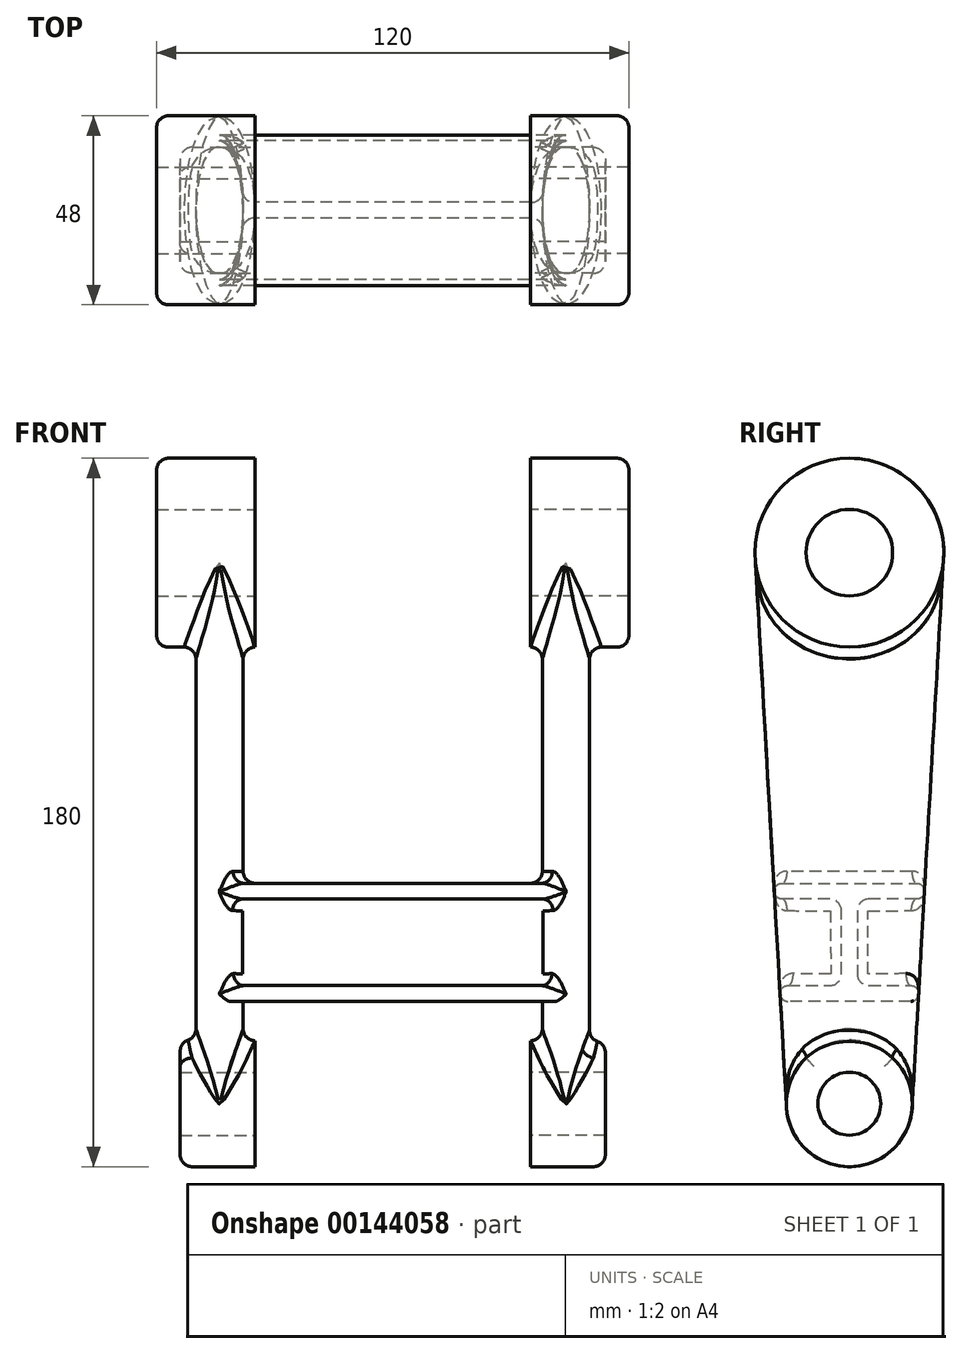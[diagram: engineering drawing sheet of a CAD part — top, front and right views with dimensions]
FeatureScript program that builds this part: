
annotation { "Feature Type Name" : "Feature", "Feature Type Description" : "" }
export const myFeature = defineFeature(function(context is Context, id is Id, definition is map)
    precondition{}
    {
        {
            assignVariable(context, id + "F0", {"name" : "gap", "anyValue" : 70 * mm});
        }
        {
            var Q0;
            Q0=qCreatedBy(makeId("Right.planeOp"),FACE);
            var sketch = newSketch(context, id + "F1", { "sketchPlane" : qUnion([Q0])});
            skCircle(sketch, "E0", {"center": v(0, 0) * mm, "radius": 8 * mm});
            skCircle(sketch, "E1", {"center": v(0, 0) * mm, "radius": 16 * mm});
            skCircle(sketch, "E2", {"center": v(0, 140) * mm, "radius": 11 * mm});
            skCircle(sketch, "E3", {"center": v(0, 140) * mm, "radius": 24 * mm});
            skSolve(sketch);
        }
        {
            var Q0;
            Q0=makeQuery(id+"F1.imprint","IMPRINT",FACE,{"disambiguationData":[TD([[makeQuery(id+"F1.imprint","IMPRINT",EDGE,{"derivedFrom":sQuery(id+"F1.wireOp",EDGE,"E0")}),1.0]])]});
            var Q1;
            Q1=makeQuery(id+"F1.imprint","IMPRINT",FACE,{"disambiguationData":[TD([[makeQuery(id+"F1.imprint","IMPRINT",EDGE,{"derivedFrom":sQuery(id+"F1.wireOp",EDGE,"E0")}),-1.0]])]});
            extrude(context, id + "F2", {"entities" : qUnion([Q0, Q1]), "depth" : 19 * mm});
        }
        {
            var Q0;
            Q0=makeQuery(id+"F1.imprint","IMPRINT",FACE,{"disambiguationData":[TD([[makeQuery(id+"F1.imprint","IMPRINT",EDGE,{"derivedFrom":sQuery(id+"F1.wireOp",EDGE,"E2")}),1.0]])]});
            var Q1;
            Q1=makeQuery(id+"F1.imprint","IMPRINT",FACE,{"disambiguationData":[TD([[makeQuery(id+"F1.imprint","IMPRINT",EDGE,{"derivedFrom":sQuery(id+"F1.wireOp",EDGE,"E2")}),-1.0]])]});
            extrude(context, id + "F3", {"entities" : qUnion([Q0, Q1]), "depth" : 25 * mm});
        }
        {
            var Q0;
            Q0=qCreatedBy(makeId("Top.planeOp"),FACE);
            var sketch = newSketch(context, id + "F4", { "sketchPlane" : qUnion([Q0])});
            skEllipse(sketch, "E4", {"center": v(9, 0) * mm, "majorRadius": 16 * mm, "minorRadius": 6 * mm, "majorAxis": v(0, -1)});
            skPoint(sketch, "E5", {"position": v(3, 0) * mm});
            skLineSegment(sketch, "E6", {"start": v(0, 16) * mm, "end": v(19, 16) * mm, "construction": true});
            skSolve(sketch);
        }
        {
            var Q0;
            Q0=sQuery(id+"F1.wireOp",VERTEX,"E3.center");
            var Q1;
            Q1=qCreatedBy(makeId("Top.planeOp"),FACE);
            cPlane(context, id + "F5", {"entities" : qUnion([Q0, Q1]), "cplaneType" : CPlaneType.PLANE_POINT, "offset" : 25 * mm, "width" : 150 * mm, "height" : 150 * mm});
        }
        {
            var Q0;
            Q0=qCreatedBy(id+"F5.planeOp",FACE);
            var sketch = newSketch(context, id + "F6", { "sketchPlane" : qUnion([Q0])});
            skEllipse(sketch, "E7", {"center": v(9, 0) * mm, "majorRadius": 24 * mm, "minorRadius": 6 * mm, "majorAxis": v(0, 1)});
            skPoint(sketch, "E8", {"position": v(3, 0) * mm});
            skLineSegment(sketch, "E9", {"start": v(0, 24) * mm, "end": v(25, 24) * mm, "construction": true});
            skSolve(sketch);
        }
        {
            var Q0;
            Q0=makeQuery(id+"F6.imprint","IMPRINT",FACE,{"disambiguationData":[TD([[makeQuery(id+"F6.imprint","IMPRINT",EDGE,{"derivedFrom":sQuery(id+"F6.wireOp",EDGE,"E7")}),1.0]])]});
            var Q1;
            Q1=makeQuery(id+"F4.imprint","IMPRINT",FACE,{"disambiguationData":[TD([[makeQuery(id+"F4.imprint","IMPRINT",EDGE,{"derivedFrom":sQuery(id+"F4.wireOp",EDGE,"E4")}),1.0]])]});
            loft(context, id + "F7", {"operationType" : NewBodyOperationType.ADD, "sheetProfilesArray" : [{ "sheetProfileEntities" : qUnion([Q0]) }, { "sheetProfileEntities" : qUnion([Q1]) }]});
        }
        {
            var Q0;
            Q0=makeQuery(id+"F1.imprint","IMPRINT",FACE,{"disambiguationData":[TD([[makeQuery(id+"F1.imprint","IMPRINT",EDGE,{"derivedFrom":sQuery(id+"F1.wireOp",EDGE,"E2")}),1.0]])]});
            var Q1;
            Q1=makeQuery(id+"F1.imprint","IMPRINT",FACE,{"disambiguationData":[TD([[makeQuery(id+"F1.imprint","IMPRINT",EDGE,{"derivedFrom":sQuery(id+"F1.wireOp",EDGE,"E0")}),1.0]])]});
            extrude(context, id + "F8", {"entities" : qUnion([Q0, Q1]), "operationType" : NewBodyOperationType.REMOVE, "depth" : 25 * mm});
        }
        {
            var Q0;
            Q0=sQuery(id+"F4.wireOp",VERTEX,"E4.center");
            var Q1;
            Q1=qCreatedBy(makeId("Right.planeOp"),FACE);
            cPlane(context, id + "F9", {"entities" : qUnion([Q0, Q1]), "cplaneType" : CPlaneType.PLANE_POINT, "offset" : 25 * mm, "width" : 150 * mm, "height" : 150 * mm});
        }
        {
            var Q0;
            Q0=qCreatedBy(makeId("Right.planeOp"),FACE);
            cPlane(context, id + "F10", {"entities" : qUnion([Q0]), "cplaneType" : CPlaneType.OFFSET, "offset" : getVariable(context, 'gap') / 2, "oppositeDirection" : true, "width" : 150 * mm, "height" : 150 * mm});
        }
        {
            var Q0;
            Q0=makeQuery(id+"F2.opExtrude","SWEPT_BODY",BODY,{"disambiguationData":[OSD([sQuery(id+"F1.wireOp",EDGE,"E1")])]});
            var Q1;
            Q1=qCreatedBy(id+"F10.planeOp",FACE);
            mirror(context, id + "F11", {"entities" : qUnion([Q0]), "mirrorPlane" : qUnion([Q1])});
        }
        {
            var Q0;
            Q0=qCreatedBy(makeId("Right.planeOp"),FACE);
            var sketch = newSketch(context, id + "F12", { "sketchPlane" : qUnion([Q0])});
            skLineSegment(sketch, "E10", {"start": v(23.96, 138.63) * mm, "end": v(15.97, -0.91) * mm, "construction": true});
            skLineSegment(sketch, "E11", {"start": v(17.51, 26) * mm, "end": v(-15.6, 26) * mm});
            skLineSegment(sketch, "E12", {"start": v(-15.6, 26) * mm, "end": v(-15.6, 30) * mm, "construction": true});
            skLineSegment(sketch, "E13", {"start": v(-15.6, 30) * mm, "end": v(-5, 30) * mm});
            skLineSegment(sketch, "E14", {"start": v(-2, 33) * mm, "end": v(-2, 49) * mm});
            skLineSegment(sketch, "E15", {"start": v(-5, 52) * mm, "end": v(-17.1, 52) * mm});
            skLineSegment(sketch, "E16", {"start": v(-17.1, 52) * mm, "end": v(-17.1, 56) * mm, "construction": true});
            skLineSegment(sketch, "E17", {"start": v(-17.1, 56) * mm, "end": v(17.11, 56) * mm});
            skLineSegment(sketch, "E18", {"start": v(17.11, 52) * mm, "end": v(5, 52) * mm});
            skLineSegment(sketch, "E19", {"start": v(2, 49) * mm, "end": v(2, 33) * mm});
            skLineSegment(sketch, "E20", {"start": v(5, 30) * mm, "end": v(17.74, 30) * mm});
            skLineSegment(sketch, "E21", {"start": v(15.63, 30) * mm, "end": v(15.63, 26) * mm, "construction": true});
            skLineSegment(sketch, "E22", {"start": v(-23.96, 138.62) * mm, "end": v(-16, 0) * mm, "construction": true});
            skPoint(sketch, "E23.visualSharp", {"position": v(0, 52) * mm});
            skArc(sketch, "E23.filletArc", {"start": v(5, 52) * mm, "mid": v(2.88, 51.12) * mm, "end": v(2, 49) * mm});
            skPoint(sketch, "E24.visualSharp", {"position": v(-2, 52) * mm});
            skArc(sketch, "E24.filletArc", {"start": v(-2, 49) * mm, "mid": v(-2.88, 51.12) * mm, "end": v(-5, 52) * mm});
            skPoint(sketch, "E25.visualSharp", {"position": v(-2, 30) * mm});
            skArc(sketch, "E25.filletArc", {"start": v(-5, 30) * mm, "mid": v(-2.88, 30.88) * mm, "end": v(-2, 33) * mm});
            skPoint(sketch, "E26.visualSharp", {"position": v(2, 30) * mm});
            skArc(sketch, "E26.filletArc", {"start": v(2, 33) * mm, "mid": v(2.88, 30.88) * mm, "end": v(5, 30) * mm});
            skPoint(sketch, "E27.endSnap0", {"position": v(0, 56) * mm});
            skLineSegment(sketch, "E28", {"start": v(0, 0) * mm, "end": v(0, 93.69) * mm, "construction": true});
            skArc(sketch, "E29", {"start": v(-15.6, 30) * mm, "mid": v(-17.6, 28) * mm, "end": v(-15.6, 26) * mm});
            skArc(sketch, "E30", {"start": v(-17.1, 56) * mm, "mid": v(-19.1, 54) * mm, "end": v(-17.1, 52) * mm});
            skArc(sketch, "E31", {"start": v(17.11, 52) * mm, "mid": v(19.11, 54) * mm, "end": v(17.11, 56) * mm});
            skLineSegment(sketch, "E32", {"start": v(17.11, 52) * mm, "end": v(17.11, 56) * mm, "construction": true});
            skArc(sketch, "E33", {"start": v(15.63, 26) * mm, "mid": v(17.63, 28) * mm, "end": v(15.63, 30) * mm});
            skSolve(sketch);
        }
        {
            var Q0;
            Q0 = qSketchRegion(id + "F12", true);
            var Q1;
            Q1=qCreatedBy(id+"F9.planeOp",FACE);
            var Q2;
            Q2=qCreatedBy(id+"F10.planeOp",FACE);
            var Q3;
            Q3=makeQuery(id+"F11.opPattern","COPY",BODY,{"derivedFrom":makeQuery(id+"F2.opExtrude","SWEPT_BODY",BODY,{"disambiguationData":[OSD([sQuery(id+"F1.wireOp",EDGE,"E1")])]}),"instanceName":"1"});
            extrude(context, id + "F13", {"entities" : qUnion([Q0]), "operationType" : NewBodyOperationType.ADD, "endBound" : BoundingType.UP_TO_SURFACE, "endBoundEntityFace" : qUnion([Q1]), "depth" : 30 * mm, "hasSecondDirection" : true, "secondDirectionBound" : SecondDirectionBoundingType.UP_TO_SURFACE, "secondDirectionOppositeDirection" : true, "secondDirectionBoundEntityFace" : qUnion([Q2]), "secondDirectionBoundEntityBody" : qUnion([Q3]), "secondDirectionDepth" : 25 * mm});
        }
        {
            var Q0;
            Q0=makeQuery(id+"F13.boolean.opBoolean","INTERSECT",EDGE,{"derivedFrom":[makeQuery(id+"F7.opLoft","SWEPT_FACE",FACE,{"disambiguationData":[OSD([sQuery(id+"F4.wireOp",EDGE,"E4"),sQuery(id+"F6.wireOp",EDGE,"E7")])]}),makeQuery(id+"F13.opExtrude","SWEPT_FACE",FACE,{"disambiguationData":[OSD([sQuery(id+"F12.wireOp",EDGE,"E17")])]})]});
            fillet(context, id + "F14", {"entities" : qUnion([Q0]), "radius" : 3 * mm, "tangentPropagation" : true, "allowEdgeOverflow" : false});
        }
        {
            var Q0;
            Q0=makeQuery(id+"F13.boolean.opBoolean","INTERSECT",EDGE,{"derivedFrom":[makeQuery(id+"F7.opLoft","SWEPT_FACE",FACE,{"disambiguationData":[OSD([sQuery(id+"F4.wireOp",EDGE,"E4"),sQuery(id+"F6.wireOp",EDGE,"E7")])]}),makeQuery(id+"F13.opExtrude","SWEPT_FACE",FACE,{"disambiguationData":[OSD([sQuery(id+"F12.wireOp",EDGE,"E13")])]})]});
            var Q1;
            Q1=makeQuery(id+"F13.boolean.opBoolean","INTERSECT",EDGE,{"derivedFrom":[makeQuery(id+"F7.opLoft","SWEPT_FACE",FACE,{"disambiguationData":[OSD([sQuery(id+"F4.wireOp",EDGE,"E4"),sQuery(id+"F6.wireOp",EDGE,"E7")])]}),makeQuery(id+"F13.opExtrude","SWEPT_FACE",FACE,{"disambiguationData":[OSD([sQuery(id+"F12.wireOp",EDGE,"E14")])]})]});
            var Q2;
            Q2=makeQuery(id+"F13.boolean.opBoolean","INTERSECT",EDGE,{"derivedFrom":[makeQuery(id+"F7.opLoft","SWEPT_FACE",FACE,{"disambiguationData":[OSD([sQuery(id+"F4.wireOp",EDGE,"E4"),sQuery(id+"F6.wireOp",EDGE,"E7")])]}),makeQuery(id+"F13.opExtrude","SWEPT_FACE",FACE,{"disambiguationData":[OSD([sQuery(id+"F12.wireOp",EDGE,"E20")])]})]});
            var Q3;
            Q3=makeQuery(id+"F13.boolean.opBoolean","INTERSECT",EDGE,{"derivedFrom":[makeQuery(id+"F7.opLoft","SWEPT_FACE",FACE,{"disambiguationData":[OSD([sQuery(id+"F4.wireOp",EDGE,"E4"),sQuery(id+"F6.wireOp",EDGE,"E7")])]}),makeQuery(id+"F13.opExtrude","SWEPT_FACE",FACE,{"disambiguationData":[OSD([sQuery(id+"F12.wireOp",EDGE,"E19")])]})]});
            fillet(context, id + "F15", {"entities" : qUnion([Q0, Q1, Q2, Q3]), "radius" : 3 * mm, "tangentPropagation" : true, "allowEdgeOverflow" : false});
        }
        {
            var Q0;
            Q0=makeQuery(id+"F2.opExtrude","SWEPT_BODY",BODY,{"disambiguationData":[OSD([sQuery(id+"F1.wireOp",EDGE,"E1")])]});
            var Q1;
            Q1=qCreatedBy(id+"F10.planeOp",FACE);
            mirror(context, id + "F16", {"operationType" : NewBodyOperationType.ADD, "entities" : qUnion([Q0]), "mirrorPlane" : qUnion([Q1])});
        }
        {
            var Q0;
            Q0=makeQuery(id+"F3.opExtrude","CAP_EDGE",EDGE,{"disambiguationData":[OSD([sQuery(id+"F1.wireOp",EDGE,"E3")])],"isStart":false});
            var Q1;
            Q1=makeQuery(id+"F16.opPattern","COPY",EDGE,{"derivedFrom":makeQuery(id+"F3.opExtrude","CAP_EDGE",EDGE,{"disambiguationData":[OSD([sQuery(id+"F1.wireOp",EDGE,"E3")])],"isStart":false}),"instanceName":"1"});
            var Q2;
            Q2=makeQuery(id+"F2.opExtrude","CAP_EDGE",EDGE,{"disambiguationData":[OSD([sQuery(id+"F1.wireOp",EDGE,"E1")])],"isStart":false});
            var Q3;
            Q3=makeQuery(id+"F16.opPattern","COPY",EDGE,{"derivedFrom":makeQuery(id+"F2.opExtrude","CAP_EDGE",EDGE,{"disambiguationData":[OSD([sQuery(id+"F1.wireOp",EDGE,"E1")])],"isStart":false}),"instanceName":"1"});
            fillet(context, id + "F17", {"entities" : qUnion([Q0, Q1, Q2, Q3]), "radius" : 3 * mm, "tangentPropagation" : true, "allowEdgeOverflow" : false});
        }
        {
            var Q0;
            Q0=makeQuery(id+"F7.boolean.opBoolean","INTERSECT",EDGE,{"derivedFrom":[makeQuery(id+"F3.opExtrude","SWEPT_FACE",FACE,{"disambiguationData":[OSD([sQuery(id+"F1.wireOp",EDGE,"E3")])]}),makeQuery(id+"F7.opLoft","SWEPT_FACE",FACE,{"disambiguationData":[OSD([sQuery(id+"F4.wireOp",EDGE,"E4"),sQuery(id+"F6.wireOp",EDGE,"E7")])]})]});
            var Q1;
            Q1=makeQuery(id+"F11.opPattern","COPY",EDGE,{"derivedFrom":makeQuery(id+"F7.boolean.opBoolean","INTERSECT",EDGE,{"derivedFrom":[makeQuery(id+"F3.opExtrude","SWEPT_FACE",FACE,{"disambiguationData":[OSD([sQuery(id+"F1.wireOp",EDGE,"E3")])]}),makeQuery(id+"F7.opLoft","SWEPT_FACE",FACE,{"disambiguationData":[OSD([sQuery(id+"F4.wireOp",EDGE,"E4"),sQuery(id+"F6.wireOp",EDGE,"E7")])]})]}),"instanceName":"1"});
            var Q2;
            Q2=makeQuery(id+"F11.opPattern","COPY",EDGE,{"derivedFrom":makeQuery(id+"F7.boolean.opBoolean","INTERSECT",EDGE,{"derivedFrom":[makeQuery(id+"F2.opExtrude","SWEPT_FACE",FACE,{"disambiguationData":[OSD([sQuery(id+"F1.wireOp",EDGE,"E1")])]}),makeQuery(id+"F7.opLoft","SWEPT_FACE",FACE,{"disambiguationData":[OSD([sQuery(id+"F4.wireOp",EDGE,"E4"),sQuery(id+"F6.wireOp",EDGE,"E7")])]})]}),"instanceName":"1"});
            var Q3;
            Q3=makeQuery(id+"F7.boolean.opBoolean","INTERSECT",EDGE,{"derivedFrom":[makeQuery(id+"F2.opExtrude","SWEPT_FACE",FACE,{"disambiguationData":[OSD([sQuery(id+"F1.wireOp",EDGE,"E1")])]}),makeQuery(id+"F7.opLoft","SWEPT_FACE",FACE,{"disambiguationData":[OSD([sQuery(id+"F4.wireOp",EDGE,"E4"),sQuery(id+"F6.wireOp",EDGE,"E7")])]})]});
            fillet(context, id + "F18", {"entities" : qUnion([Q0, Q1, Q2, Q3]), "radius" : 3 * mm, "tangentPropagation" : true, "allowEdgeOverflow" : false});
        }
        {
            var Q0;
            Q0=makeQuery(id+"F11.opPattern","COPY",EDGE,{"derivedFrom":makeQuery(id+"F2.opExtrude","CAP_EDGE",EDGE,{"disambiguationData":[OSD([sQuery(id+"F1.wireOp",EDGE,"E1")])],"isStart":false}),"instanceName":"1"});
            var Q1;
            Q1=makeQuery(id+"F11.opPattern","COPY",EDGE,{"derivedFrom":makeQuery(id+"F3.opExtrude","CAP_EDGE",EDGE,{"disambiguationData":[OSD([sQuery(id+"F1.wireOp",EDGE,"E3")])],"isStart":false}),"instanceName":"1"});
            fillet(context, id + "F19", {"entities" : qUnion([Q0, Q1]), "radius" : 3 * mm, "tangentPropagation" : true, "allowEdgeOverflow" : false});
        }
    });
